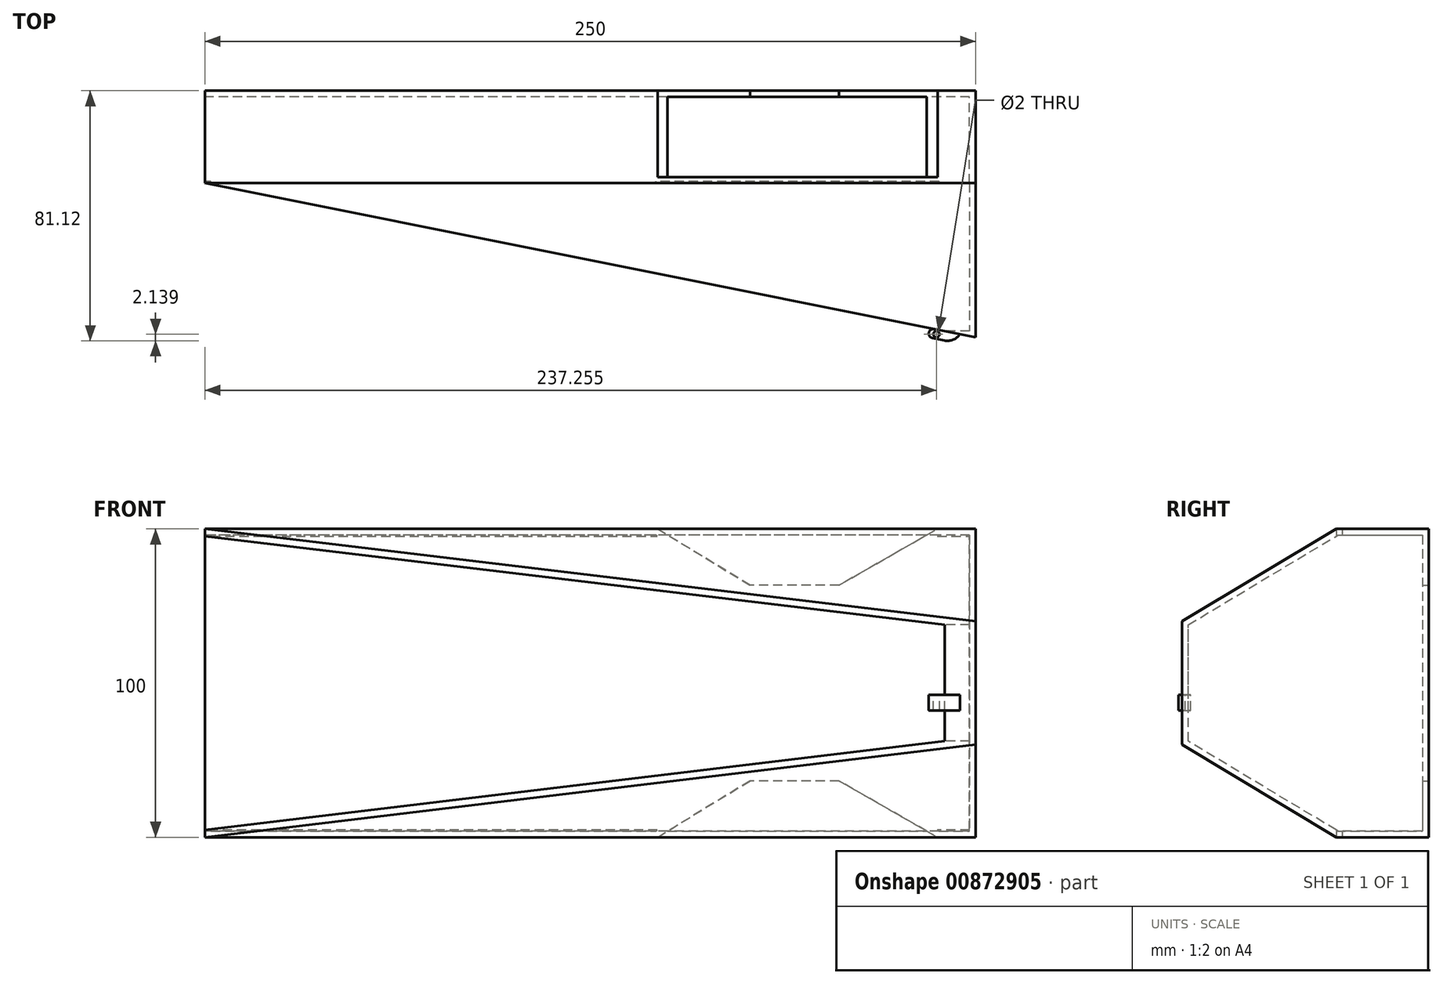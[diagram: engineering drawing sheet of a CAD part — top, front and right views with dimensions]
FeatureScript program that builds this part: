
annotation { "Feature Type Name" : "Feature", "Feature Type Description" : "" }
export const myFeature = defineFeature(function(context is Context, id is Id, definition is map)
    precondition{}
    {
        {
            var Q0;
            Q0=qCreatedBy(makeId("Front.planeOp"),FACE);
            var sketch = newSketch(context, id + "F0", { "sketchPlane" : qUnion([Q0])});
            skLineSegment(sketch, "E0.bottom", {"start": v(-126.72, 60.76) * mm, "end": v(20.07, 60.76) * mm});
            skLineSegment(sketch, "E0.left", {"start": v(-126.72, 60.76) * mm, "end": v(-126.72, 10.76) * mm});
            skLineSegment(sketch, "E0.right", {"start": v(123.28, 60.76) * mm, "end": v(123.28, 10.76) * mm});
            skLineSegment(sketch, "E1", {"start": v(20.07, 60.76) * mm, "end": v(50.14, 42.48) * mm});
            skLineSegment(sketch, "E2", {"start": v(50.14, 42.48) * mm, "end": v(78.96, 42.48) * mm});
            skLineSegment(sketch, "E3", {"start": v(78.96, 42.48) * mm, "end": v(110.88, 60.76) * mm});
            skLineSegment(sketch, "E4.trimOffspring", {"start": v(110.88, 60.76) * mm, "end": v(123.28, 60.76) * mm});
            skLineSegment(sketch, "E5.MirrorCS", {"start": v(110.88, -39.24) * mm, "end": v(123.28, -39.24) * mm});
            skLineSegment(sketch, "E6.MirrorCS", {"start": v(123.28, -39.24) * mm, "end": v(123.28, 10.76) * mm});
            skLineSegment(sketch, "E7.MirrorCS", {"start": v(50.14, -20.95) * mm, "end": v(78.96, -20.95) * mm});
            skLineSegment(sketch, "E8.MirrorCS", {"start": v(78.96, -20.95) * mm, "end": v(110.88, -39.24) * mm});
            skLineSegment(sketch, "E9.MirrorCS", {"start": v(20.07, -39.24) * mm, "end": v(50.14, -20.95) * mm});
            skLineSegment(sketch, "E10.MirrorCS", {"start": v(-126.72, -39.24) * mm, "end": v(-126.72, 10.76) * mm});
            skLineSegment(sketch, "E11.MirrorCS", {"start": v(-126.72, -39.24) * mm, "end": v(20.07, -39.24) * mm});
            skSolve(sketch);
        }
        {
            var Q0;
            Q0=makeQuery(id+"F0.imprint","IMPRINT",FACE,{"disambiguationData":[TD([[makeQuery(id+"F0.imprint","IMPRINT",EDGE,{"derivedFrom":sQuery(id+"F0.wireOp",EDGE,"E0.bottom")}),-1.0]])]});
            extrude(context, id + "F1", {"entities" : qUnion([Q0]), "depth" : 5 * mm, "offsetDistance" : 25 * mm});
        }
        {
            var Q0;
            Q0=makeQuery(id+"F1.opExtrude","CAP_FACE",FACE,{"disambiguationData":[OSD([sQuery(id+"F0.wireOp",EDGE,"E0.bottom"),sQuery(id+"F0.wireOp",EDGE,"E0.left"),sQuery(id+"F0.wireOp",EDGE,"E0.right"),sQuery(id+"F0.wireOp",EDGE,"E1"),sQuery(id+"F0.wireOp",EDGE,"E2"),sQuery(id+"F0.wireOp",EDGE,"E3"),sQuery(id+"F0.wireOp",EDGE,"E4.trimOffspring"),sQuery(id+"F0.wireOp",EDGE,"E5.MirrorCS"),sQuery(id+"F0.wireOp",EDGE,"E6.MirrorCS"),sQuery(id+"F0.wireOp",EDGE,"E7.MirrorCS"),sQuery(id+"F0.wireOp",EDGE,"E8.MirrorCS"),sQuery(id+"F0.wireOp",EDGE,"E9.MirrorCS"),sQuery(id+"F0.wireOp",EDGE,"E10.MirrorCS"),sQuery(id+"F0.wireOp",EDGE,"E11.MirrorCS")])],"isStart":false});
            var sketch = newSketch(context, id + "F2", { "sketchPlane" : qUnion([Q0])});
            skLineSegment(sketch, "E12.0", {"start": v(19.51, -37.24) * mm, "end": v(49.57, -18.95) * mm});
            skLineSegment(sketch, "E12.1", {"start": v(121.28, 58.76) * mm, "end": v(111.4, 58.76) * mm});
            skLineSegment(sketch, "E12.2", {"start": v(121.28, -37.24) * mm, "end": v(121.28, 58.76) * mm});
            skLineSegment(sketch, "E12.3", {"start": v(111.4, -37.24) * mm, "end": v(121.28, -37.24) * mm});
            skLineSegment(sketch, "E12.4", {"start": v(79.49, -18.95) * mm, "end": v(111.4, -37.24) * mm});
            skLineSegment(sketch, "E12.5", {"start": v(111.4, 58.76) * mm, "end": v(79.49, 40.48) * mm});
            skLineSegment(sketch, "E12.6", {"start": v(49.57, -18.95) * mm, "end": v(79.49, -18.95) * mm});
            skLineSegment(sketch, "E12.7", {"start": v(79.49, 40.48) * mm, "end": v(49.57, 40.48) * mm});
            skLineSegment(sketch, "E12.8", {"start": v(49.57, 40.48) * mm, "end": v(19.51, 58.76) * mm});
            skLineSegment(sketch, "E12.9", {"start": v(19.51, 58.76) * mm, "end": v(-124.72, 58.76) * mm});
            skLineSegment(sketch, "E12.10", {"start": v(-124.72, 58.76) * mm, "end": v(-124.72, -37.24) * mm});
            skLineSegment(sketch, "E12.11", {"start": v(-124.72, -37.24) * mm, "end": v(19.51, -37.24) * mm});
            skLineSegment(sketch, "E13.0", {"start": v(20.07, -39.24) * mm, "end": v(50.14, -20.95) * mm});
            skLineSegment(sketch, "E13.1", {"start": v(123.28, 60.76) * mm, "end": v(110.88, 60.76) * mm});
            skLineSegment(sketch, "E13.2", {"start": v(123.28, -39.24) * mm, "end": v(123.28, 60.76) * mm});
            skLineSegment(sketch, "E13.3", {"start": v(110.88, -39.24) * mm, "end": v(123.28, -39.24) * mm});
            skLineSegment(sketch, "E13.4", {"start": v(78.96, -20.95) * mm, "end": v(110.88, -39.24) * mm});
            skLineSegment(sketch, "E13.5", {"start": v(110.88, 60.76) * mm, "end": v(78.96, 42.48) * mm});
            skLineSegment(sketch, "E13.6", {"start": v(50.14, -20.95) * mm, "end": v(78.96, -20.95) * mm});
            skLineSegment(sketch, "E13.7", {"start": v(78.96, 42.48) * mm, "end": v(50.14, 42.48) * mm});
            skLineSegment(sketch, "E13.8", {"start": v(50.14, 42.48) * mm, "end": v(20.07, 60.76) * mm});
            skLineSegment(sketch, "E13.9", {"start": v(20.07, 60.76) * mm, "end": v(-126.72, 60.76) * mm});
            skLineSegment(sketch, "E13.10", {"start": v(-126.72, 60.76) * mm, "end": v(-126.72, -39.24) * mm});
            skLineSegment(sketch, "E13.11", {"start": v(-126.72, -39.24) * mm, "end": v(20.07, -39.24) * mm});
            skSolve(sketch);
        }
        {
            var Q0;
            Q0=makeQuery(id+"F2.imprint","IMPRINT",FACE,{"disambiguationData":[TD([[makeQuery(id+"F2.imprint","IMPRINT",EDGE,{"derivedFrom":sQuery(id+"F2.wireOp",EDGE,"E12.0")}),-1.0]])]});
            extrude(context, id + "F3", {"entities" : qUnion([Q0]), "operationType" : NewBodyOperationType.ADD, "depth" : 25 * mm, "offsetDistance" : 25 * mm});
        }
        {
            var Q0;
            Q0=makeQuery(id+"F3.opExtrude","CAP_FACE",FACE,{"disambiguationData":[OSD([sQuery(id+"F2.wireOp",EDGE,"E12.0"),sQuery(id+"F2.wireOp",EDGE,"E12.1"),sQuery(id+"F2.wireOp",EDGE,"E12.2"),sQuery(id+"F2.wireOp",EDGE,"E12.3"),sQuery(id+"F2.wireOp",EDGE,"E12.4"),sQuery(id+"F2.wireOp",EDGE,"E12.5"),sQuery(id+"F2.wireOp",EDGE,"E12.6"),sQuery(id+"F2.wireOp",EDGE,"E12.7"),sQuery(id+"F2.wireOp",EDGE,"E12.8"),sQuery(id+"F2.wireOp",EDGE,"E12.9"),sQuery(id+"F2.wireOp",EDGE,"E12.10"),sQuery(id+"F2.wireOp",EDGE,"E12.11"),sQuery(id+"F2.wireOp",EDGE,"E13.0"),sQuery(id+"F2.wireOp",EDGE,"E13.1"),sQuery(id+"F2.wireOp",EDGE,"E13.2"),sQuery(id+"F2.wireOp",EDGE,"E13.3"),sQuery(id+"F2.wireOp",EDGE,"E13.4"),sQuery(id+"F2.wireOp",EDGE,"E13.5"),sQuery(id+"F2.wireOp",EDGE,"E13.6"),sQuery(id+"F2.wireOp",EDGE,"E13.7"),sQuery(id+"F2.wireOp",EDGE,"E13.8"),sQuery(id+"F2.wireOp",EDGE,"E13.9"),sQuery(id+"F2.wireOp",EDGE,"E13.10"),sQuery(id+"F2.wireOp",EDGE,"E13.11")])],"isStart":false});
            var sketch = newSketch(context, id + "F4", { "sketchPlane" : qUnion([Q0])});
            skLineSegment(sketch, "E14", {"start": v(20.07, -39.24) * mm, "end": v(110.88, -39.24) * mm});
            skLineSegment(sketch, "E15", {"start": v(110.88, 60.76) * mm, "end": v(20.07, 60.76) * mm});
            skSolve(sketch);
        }
        {
            var Q0;
            Q0=makeQuery(id+"F4.imprint","IMPRINT",FACE,{"disambiguationData":[TD([[makeQuery(id+"F4.imprint","IMPRINT",EDGE,{"derivedFrom":sQuery(id+"F4.wireOp",EDGE,"E15")}),1.0]])]});
            var Q1;
            Q1=makeQuery(id+"F4.imprint","IMPRINT",FACE,{"disambiguationData":[TD([[makeQuery(id+"F4.imprint","IMPRINT",EDGE,{"derivedFrom":sQuery(id+"F4.wireOp",EDGE,"E14")}),1.0]])]});
            extrude(context, id + "F5", {"entities" : qUnion([Q0, Q1]), "operationType" : NewBodyOperationType.ADD, "depth" : -2 * mm, "offsetDistance" : 25 * mm});
        }
        {
            var Q0;
            Q0=makeQuery(id+"F3.boolean.opBoolean","MERGE",FACE,{"derivedFrom":[makeQuery(id+"F1.opExtrude","SWEPT_FACE",FACE,{"disambiguationData":[OSD([sQuery(id+"F0.wireOp",EDGE,"E0.right"),sQuery(id+"F0.wireOp",EDGE,"E6.MirrorCS")])]}),makeQuery(id+"F3.opExtrude","SWEPT_FACE",FACE,{"disambiguationData":[OSD([sQuery(id+"F2.wireOp",EDGE,"E13.2")])]})]});
            var sketch = newSketch(context, id + "F6", { "sketchPlane" : qUnion([Q0])});
            skLineSegment(sketch, "E16", {"start": v(-30, -39.24) * mm, "end": v(-80, -9.24) * mm});
            skLineSegment(sketch, "E17", {"start": v(-80, -9.24) * mm, "end": v(-80, 30.76) * mm});
            skLineSegment(sketch, "E18", {"start": v(-80, 30.76) * mm, "end": v(-30, 60.76) * mm});
            skSolve(sketch);
        }
        {
            var Q0;
            Q0=makeQuery(id+"F6.imprint","IMPRINT",FACE,{"disambiguationData":[TD([[makeQuery(id+"F6.imprint","IMPRINT",EDGE,{"derivedFrom":sQuery(id+"F6.wireOp",EDGE,"E16")}),-1.0]])]});
            extrude(context, id + "F7", {"entities" : qUnion([Q0]), "operationType" : NewBodyOperationType.ADD, "depth" : -250 * mm, "offsetDistance" : 25 * mm});
        }
        {
            var Q0;
            Q0=makeQuery(id+"F7.boolean.opBoolean","MERGE",FACE,{"derivedFrom":[makeQuery(id+"F3.boolean.opBoolean","MERGE",FACE,{"derivedFrom":[makeQuery(id+"F1.opExtrude","SWEPT_FACE",FACE,{"disambiguationData":[OSD([sQuery(id+"F0.wireOp",EDGE,"E0.left"),sQuery(id+"F0.wireOp",EDGE,"E10.MirrorCS")])]}),makeQuery(id+"F3.opExtrude","SWEPT_FACE",FACE,{"disambiguationData":[OSD([sQuery(id+"F2.wireOp",EDGE,"E13.10")])]})]}),makeQuery(id+"F7.opExtrude","CAP_FACE",FACE,{"disambiguationData":[OSD([sQuery(id+"F2.wireOp",EDGE,"E13.2"),sQuery(id+"F6.wireOp",EDGE,"E16"),sQuery(id+"F6.wireOp",EDGE,"E17"),sQuery(id+"F6.wireOp",EDGE,"E18")])],"isStart":false})]});
            var sketch = newSketch(context, id + "F8", { "sketchPlane" : qUnion([Q0])});
            skLineSegment(sketch, "E19.0", {"start": v(29.45, 58.76) * mm, "end": v(2, 58.76) * mm});
            skLineSegment(sketch, "E19.1", {"start": v(2, -37.24) * mm, "end": v(29.45, -37.24) * mm});
            skLineSegment(sketch, "E19.2", {"start": v(29.45, -37.24) * mm, "end": v(78, -8.1) * mm});
            skLineSegment(sketch, "E19.3", {"start": v(2, 58.76) * mm, "end": v(2, -37.24) * mm});
            skLineSegment(sketch, "E19.4", {"start": v(78, -8.1) * mm, "end": v(78, 29.63) * mm});
            skLineSegment(sketch, "E19.5", {"start": v(78, 29.63) * mm, "end": v(29.45, 58.76) * mm});
            skSolve(sketch);
        }
        {
            var Q0;
            Q0=makeQuery(id+"F8.imprint","IMPRINT",FACE,{"disambiguationData":[TD([[makeQuery(id+"F8.imprint","IMPRINT",EDGE,{"derivedFrom":sQuery(id+"F8.wireOp",EDGE,"E19.0")}),1.0]])]});
            extrude(context, id + "F9", {"entities" : qUnion([Q0]), "operationType" : NewBodyOperationType.REMOVE, "oppositeDirection" : true, "depth" : 248 * mm, "offsetDistance" : 25 * mm});
        }
        {
            var Q0;
            Q0=makeQuery(id+"F5.boolean.opBoolean","MERGE",FACE,{"derivedFrom":[makeQuery(id+"F3.boolean.opBoolean","MERGE",FACE,{"derivedFrom":[makeQuery(id+"F1.opExtrude","SWEPT_FACE",FACE,{"disambiguationData":[OSD([sQuery(id+"F0.wireOp",EDGE,"E5.MirrorCS")])]}),makeQuery(id+"F3.opExtrude","SWEPT_FACE",FACE,{"disambiguationData":[OSD([sQuery(id+"F2.wireOp",EDGE,"E13.3")])]})]}),makeQuery(id+"F3.boolean.opBoolean","MERGE",FACE,{"derivedFrom":[makeQuery(id+"F1.opExtrude","SWEPT_FACE",FACE,{"disambiguationData":[OSD([sQuery(id+"F0.wireOp",EDGE,"E11.MirrorCS")])]}),makeQuery(id+"F3.opExtrude","SWEPT_FACE",FACE,{"disambiguationData":[OSD([sQuery(id+"F2.wireOp",EDGE,"E13.11")])]})]}),makeQuery(id+"F5.opExtrude","SWEPT_FACE",FACE,{"disambiguationData":[OSD([sQuery(id+"F4.wireOp",EDGE,"E14")])]})]});
            var sketch = newSketch(context, id + "F10", { "sketchPlane" : qUnion([Q0])});
            skLineSegment(sketch, "E20", {"start": v(-126.72, 30) * mm, "end": v(123.28, 80) * mm});
            skLineSegment(sketch, "E21", {"start": v(-126.72, 30) * mm, "end": v(-126.72, 80) * mm});
            skLineSegment(sketch, "E22", {"start": v(-126.72, 80) * mm, "end": v(123.28, 80) * mm});
            skSolve(sketch);
        }
        {
            var Q0;
            Q0=makeQuery(id+"F10.imprint","IMPRINT",FACE,{"disambiguationData":[TD([[makeQuery(id+"F10.imprint","IMPRINT",EDGE,{"derivedFrom":sQuery(id+"F10.wireOp",EDGE,"E20")}),1.0]])]});
            extrude(context, id + "F11", {"entities" : qUnion([Q0]), "operationType" : NewBodyOperationType.REMOVE, "oppositeDirection" : true, "depth" : 110 * mm, "offsetDistance" : 25 * mm});
        }
        {
            var Q0;
            Q0=makeQuery(id+"F11.boolean.opBoolean","COPY",FACE,{"derivedFrom":makeQuery(id+"F11.opExtrude","SWEPT_FACE",FACE,{"disambiguationData":[OSD([sQuery(id+"F10.wireOp",EDGE,"E20")])]})});
            var sketch = newSketch(context, id + "F12", { "sketchPlane" : qUnion([Q0])});
            skLineSegment(sketch, "E23", {"start": v(-118.38, 58.43) * mm, "end": v(-118.38, -36.9) * mm});
            skSolve(sketch);
        }
        {
            var Q0;
            {var subQ0=sQuery(id+"F10.wireOp",EDGE,"E20");var subQ1=makeQuery(id+"F11.opExtrude","SWEPT_FACE",FACE,{"disambiguationData":[OSD([subQ0])]});var subQ5=sQuery(id+"F6.wireOp",EDGE,"E16");var subQ6=makeQuery(id+"F7.opExtrude","SWEPT_FACE",FACE,{"disambiguationData":[OSD([subQ5])]});Q0=makeQuery(id+"F12.imprint","IMPRINT",FACE,{"disambiguationData":[TD([[makeQuery(id+"F12.imprint","IMPRINT",EDGE,{"derivedFrom":makeQuery(id+"F11.boolean.opBoolean","INTERSECT",EDGE,{"derivedFrom":[subQ6,subQ1]})}),-1.0]])]});}
            var sketch = newSketch(context, id + "F13", { "sketchPlane" : qUnion([Q0])});
            skLineSegment(sketch, "E24.bottom", {"start": v(131.38, 1.9) * mm, "end": v(126.38, 1.9) * mm});
            skLineSegment(sketch, "E24.top", {"start": v(131.38, 6.9) * mm, "end": v(126.38, 6.9) * mm});
            skLineSegment(sketch, "E24.left", {"start": v(131.38, 1.9) * mm, "end": v(131.38, 6.9) * mm});
            skLineSegment(sketch, "E24.right", {"start": v(126.38, 1.9) * mm, "end": v(126.38, 6.9) * mm});
            skSolve(sketch);
        }
        {
            var Q0;
            Q0=makeQuery(id+"F13.imprint","IMPRINT",FACE,{"disambiguationData":[TD([[makeQuery(id+"F13.imprint","IMPRINT",EDGE,{"derivedFrom":sQuery(id+"F13.wireOp",EDGE,"E24.bottom")}),-1.0]])]});
            extrude(context, id + "F14", {"entities" : qUnion([Q0]), "operationType" : NewBodyOperationType.ADD, "depth" : 3 * mm, "offsetDistance" : 25 * mm});
        }
        {
            var Q0;
            Q0=makeQuery(id+"F14.opExtrude","CAP_EDGE",EDGE,{"disambiguationData":[OSD([sQuery(id+"F13.wireOp",EDGE,"E24.left")])],"isStart":false});
            fillet(context, id + "F15", {"entities" : qUnion([Q0]), "radius" : 5 * mm, "tangentPropagation" : true, "allowEdgeOverflow" : false});
        }
        {
            var Q0;
            Q0=makeQuery(id+"F14.opExtrude","SWEPT_FACE",FACE,{"disambiguationData":[OSD([sQuery(id+"F13.wireOp",EDGE,"E24.right")])]});
            extrude(context, id + "F16", {"entities" : qUnion([Q0]), "operationType" : NewBodyOperationType.ADD, "depth" : 5 * mm, "offsetDistance" : 25 * mm});
        }
        {
            var Q0;
            {var subQ0=sQuery(id+"F13.wireOp",EDGE,"E24.top");Q0=makeQuery(id+"F16.boolean.opBoolean","MERGE",FACE,{"derivedFrom":[makeQuery(id+"F14.opExtrude","SWEPT_FACE",FACE,{"disambiguationData":[OSD([subQ0])]}),makeQuery(id+"F16.opExtrude","SWEPT_FACE",FACE,{"disambiguationData":[OSD([sQuery(id+"F8.wireOp",EDGE,"E19.4"),sQuery(id+"F10.wireOp",EDGE,"E20"),subQ0,sQuery(id+"F13.wireOp",EDGE,"E24.right")])]})]});}
            var sketch = newSketch(context, id + "F17", { "sketchPlane" : qUnion([Q0])});
            skPoint(sketch, "E25", {"position": v(110.53, -78.98) * mm});
            skSolve(sketch);
        }
        {
            var Q0;
            Q0=sQuery(id+"F17.wireOp",VERTEX,"E25");
            var Q1;
            Q1=makeQuery(id+"F1.opExtrude","SWEPT_BODY",BODY,{"disambiguationData":[OSD([sQuery(id+"F0.wireOp",EDGE,"E0.bottom"),sQuery(id+"F0.wireOp",EDGE,"E0.left"),sQuery(id+"F0.wireOp",EDGE,"E0.right"),sQuery(id+"F0.wireOp",EDGE,"E1"),sQuery(id+"F0.wireOp",EDGE,"E2"),sQuery(id+"F0.wireOp",EDGE,"E3"),sQuery(id+"F0.wireOp",EDGE,"E4.trimOffspring"),sQuery(id+"F0.wireOp",EDGE,"E5.MirrorCS"),sQuery(id+"F0.wireOp",EDGE,"E6.MirrorCS"),sQuery(id+"F0.wireOp",EDGE,"E7.MirrorCS"),sQuery(id+"F0.wireOp",EDGE,"E8.MirrorCS"),sQuery(id+"F0.wireOp",EDGE,"E9.MirrorCS"),sQuery(id+"F0.wireOp",EDGE,"E10.MirrorCS"),sQuery(id+"F0.wireOp",EDGE,"E11.MirrorCS")])]});
            hole(context, id + "F18", {"style" : HoleStyle.SIMPLE, "endStyle" : HoleEndStyle.THROUGH, "holeDiameter" : 2 * mm, "majorDiameter" : 5 * mm, "isTappedThrough" : true, "tappedDepth" : 12 * mm, "tapClearance" : 3, "locations" : qUnion([Q0]), "scope" : qUnion([Q1])});
        }
        {
            var Q0;
            Q0=makeQuery(id+"F16.opExtrude","CAP_EDGE",EDGE,{"disambiguationData":[OSD([sQuery(id+"F13.wireOp",EDGE,"E24.right")])],"isStart":false});
            var Q1;
            Q1=makeQuery(id+"F16.opExtrude","CAP_EDGE",EDGE,{"disambiguationData":[OSD([sQuery(id+"F8.wireOp",EDGE,"E19.4"),sQuery(id+"F10.wireOp",EDGE,"E20"),sQuery(id+"F13.wireOp",EDGE,"E24.right")])],"isStart":false});
            fillet(context, id + "F19", {"entities" : qUnion([Q0, Q1]), "radius" : 1.5 * mm, "tangentPropagation" : true, "allowEdgeOverflow" : false});
        }
    });
